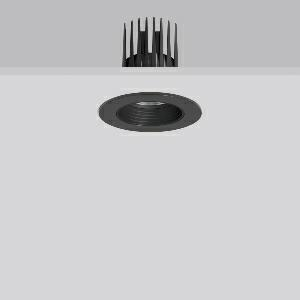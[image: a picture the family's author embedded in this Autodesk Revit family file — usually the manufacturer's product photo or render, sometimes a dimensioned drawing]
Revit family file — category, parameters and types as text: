
# Revit family: heledon_mini_e_901754_003_76_a3fb
name_source: partatom
category: Lighting Fixtures
units: mm (PartAtom-declared; Revit-internal decimal feet)

## family parameters
Cut with Voids When Loaded = No
Host = Face
Light Source = No
Part Type = Normal
Room Calculation Point = No
Round Connector Dimension = Use Diameter
Shared = No

## types (1)
- HELEDON mini E (1 x LED Modul 930, 3250 lm, 3000)
    Apparent Load = 29 VA
    Approval mark = CE
    CIE Flux Codes = 80 99 100 100 100
    Color Rendering = 90
    Color Temperature = 3000
    Default Elevation = 1800 mm
    Description = Series: HELEDON mini
Round recessed downlight. Housing: die-cast aluminium, powder-coated. Black plastic ring and recessed LED to prevent glare from the side. Optical assembly with lens made of plastic (polycarbonate) for the best homogeneous light distribution - can be changed without tools. Best colour rendering index Ra>90. Suitable for Recessed ceiling mounting. Installation without tools thanks to spring fastening system. Including separate LED converter with connecting cable 600 mm.High quality converter without flickering and stroboscopic effect. Through-wiring box (5 pole) available as accessory. The following accessories can be mounted without use of tools: interchangeable lenses, decorative glasses, honeycomb louvre, clear and frosted diffusers, white interchangeable plastic ring. 
Colour: deep black, matt (RAL 9005)
Diameter: 124 mm
Height: 3 mm
Cut-out diameter: 114 mm
Recess height: 170 mm
Luminaire: recess height: 120 mm
Lamp: LED
Socket: without socket
Colour temperature: 3000K
Colour rendering index (CRI): 92
System power: 29 W
Rated luminous flux: 3250 lm
Luminous efficiency: 112 lm/W
Control gear: Converter, dimmable, DALI
Protection class: II
Type of protection: IP 20
    Height = 0 mm  [stored 0 ft]
    Lamp = 1 x LED Modul 930
    Lamp Light Flux = 3250 lm
    Lamp count = 1
    Length = 124 mm  [stored 0.406824 ft]
    Lifetime = 50000 h
    Luminous efficacy = 112 lm/W
    Manufacturer = RZB
    ModVariant = No
    Model = 901754.003.76
    Mounting Place = Ceiling
    Mounting Type = Recessed
    Number of Poles = 1
    OnlyDefault = Yes
    Power Factor = 1
    Product Name = HELEDON mini E
    Product group = Recessed downlights
    ProductGroupID = 402
    Protection Class = Protection class II
    Protection Degree = IP 20
    RLX_Detail_Level = 1
    RLX_Emergency_Light_Flux = 0 lm
    RLX_Emergency_Type = 0
    RLX_Emergency_Type_DB = No
    RlxData = <blob elided: 129861 chars, md5=bac0bc91>
    Socket = socket
    Standby Power = 0 W
    System Light Flux = 3250 lm
    System Power = 29 W
    Type Comments = Product without accessories
    Type Image = 901656.003.jpg
    URL = http://relux.com
    VarID = ---
    Voltage = 230 V
    Voltage Range = 220-240 V
    Weight = 0.00 kg
    Width = 0 mm  [stored 0 ft]

note: [stored X ft] marks values corroborated as IEEE doubles in the binary element streams (Revit-internal decimal feet)

## geometry (parser evidence)
native form markers: Blend x4, Sweep x10
no freeform markers — native parametric forms only
